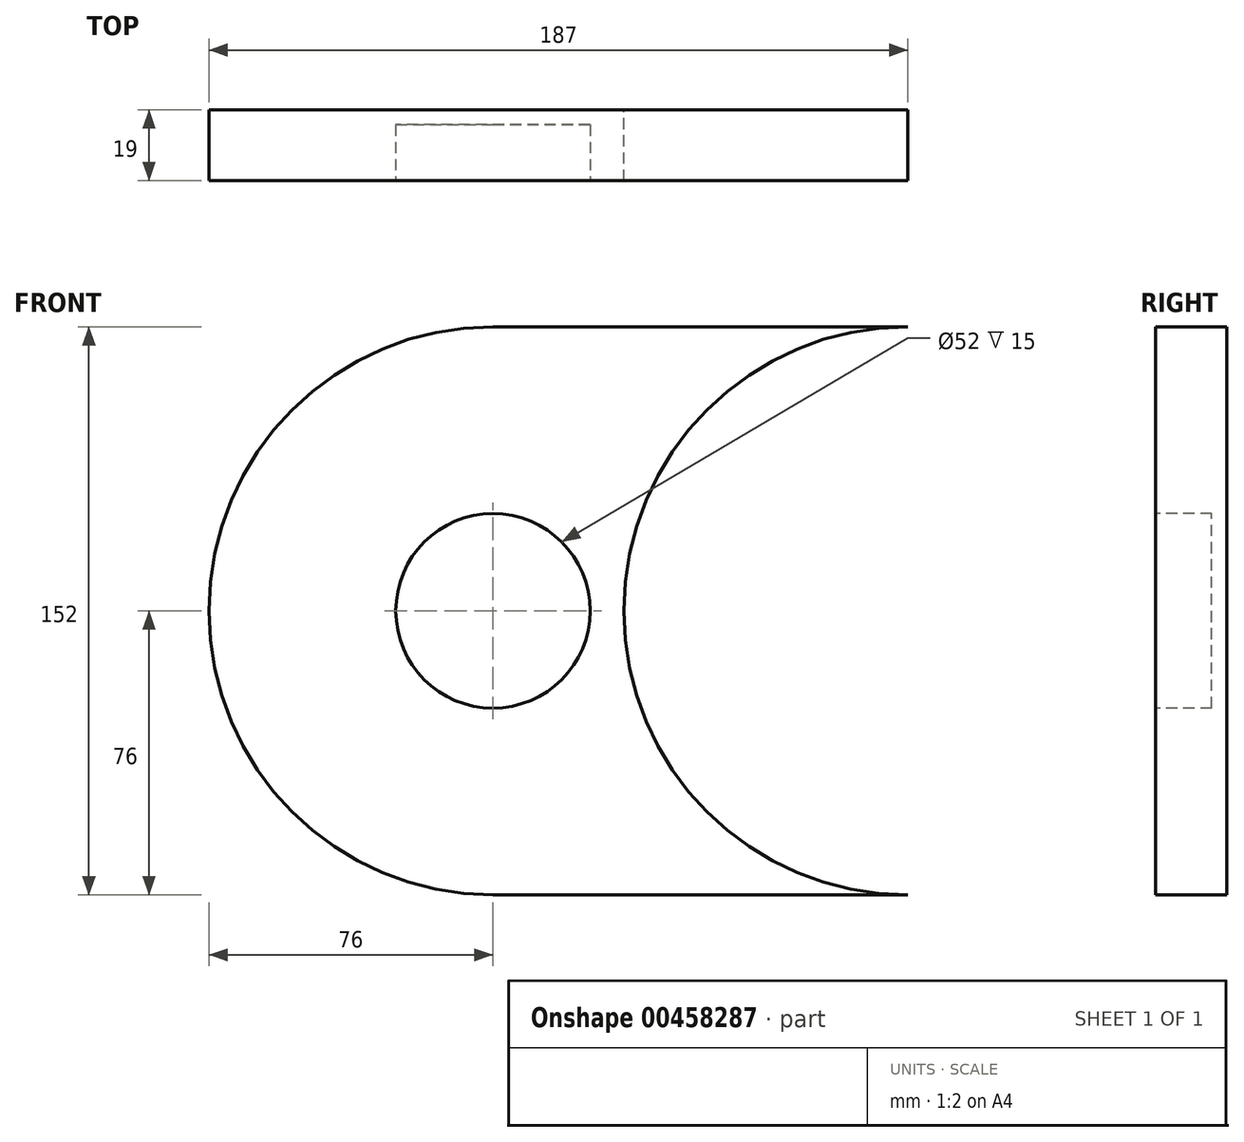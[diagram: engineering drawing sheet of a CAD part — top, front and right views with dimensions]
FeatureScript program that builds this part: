
annotation { "Feature Type Name" : "Feature", "Feature Type Description" : "" }
export const myFeature = defineFeature(function(context is Context, id is Id, definition is map)
    precondition{}
    {
        {
            var Q0;
            Q0=qCreatedBy(makeId("Front.planeOp"),FACE);
            var sketch = newSketch(context, id + "F0", { "sketchPlane" : qUnion([Q0])});
            skCircle(sketch, "E0", {"center": v(0, 0) * mm, "radius": 76 * mm});
            skCircle(sketch, "E1", {"center": v(111, 0) * mm, "radius": 76 * mm});
            skLineSegment(sketch, "E2", {"start": v(111, -76) * mm, "end": v(0, -76) * mm});
            skLineSegment(sketch, "E3", {"start": v(0, 76) * mm, "end": v(111, 76) * mm});
            skSolve(sketch);
        }
        {
            var Q0;
            {var subQ0=sQuery(id+"F0.wireOp",EDGE,"E3");Q0=makeQuery(id+"F0.imprint","IMPRINT",FACE,{"disambiguationData":[TD([[makeQuery(id+"F0.imprint","IMPRINT",EDGE,{"derivedFrom":subQ0}),-1.0]])]});}
            var Q1;
            {var subQ0=sQuery(id+"F0.wireOp",EDGE,"E2");Q1=makeQuery(id+"F0.imprint","IMPRINT",FACE,{"disambiguationData":[TD([[makeQuery(id+"F0.imprint","IMPRINT",EDGE,{"derivedFrom":subQ0}),-1.0]])]});}
            var Q2;
            {var subQ0=sQuery(id+"F0.wireOp",EDGE,"E1");var subQ1=sQuery(id+"F0.wireOp",EDGE,"E0");var subQ2=makeQuery(id+"F0.imprint","INTERSECT",VERTEX,{"disambiguationData":[OD(0.0)],"derivedFrom":[subQ1,subQ0]});Q2=makeQuery(id+"F0.imprint","IMPRINT",FACE,{"disambiguationData":[TD([[makeQuery(id+"F0.imprint","IMPRINT",EDGE,{"disambiguationData":[TD([[subQ2,1.0]])],"derivedFrom":subQ1}),1.0]])]});}
            var Q3;
            {var subQ0=sQuery(id+"F0.wireOp",EDGE,"E1");var subQ1=sQuery(id+"F0.wireOp",EDGE,"E0");var subQ2=makeQuery(id+"F0.imprint","INTERSECT",VERTEX,{"disambiguationData":[OD(0.0)],"derivedFrom":[subQ1,subQ0]});Q3=makeQuery(id+"F0.imprint","IMPRINT",FACE,{"disambiguationData":[TD([[makeQuery(id+"F0.imprint","IMPRINT",EDGE,{"disambiguationData":[TD([[subQ2,1.0]])],"derivedFrom":subQ1}),-1.0]])]});}
            var Q4;
            {var subQ0=sQuery(id+"F0.wireOp",EDGE,"E0");var subQ1=makeQuery(id+"F0.imprint","INTERSECT",VERTEX,{"derivedFrom":[subQ0,sQuery(id+"F0.wireOp",EDGE,"E3")]});Q4=makeQuery(id+"F0.imprint","IMPRINT",FACE,{"disambiguationData":[TD([[makeQuery(id+"F0.imprint","IMPRINT",EDGE,{"disambiguationData":[TD([[subQ1,1.0]])],"derivedFrom":subQ0}),1.0]])]});}
            extrude(context, id + "F1", {"entities" : qUnion([Q0, Q1, Q2, Q3, Q4]), "depth" : 50 * mm, "offsetDistance" : 25 * mm});
        }
        {
            var Q0;
            Q0=qCreatedBy(makeId("Front.planeOp"),FACE);
            cPlane(context, id + "F2", {"entities" : qUnion([Q0]), "cplaneType" : CPlaneType.OFFSET, "offset" : 19 * mm, "width" : 150 * mm, "height" : 150 * mm});
        }
        {
            var Q0;
            Q0=qCreatedBy(id+"F2.planeOp",FACE);
            var sketch = newSketch(context, id + "F3", { "sketchPlane" : qUnion([Q0])});
            skCircle(sketch, "E4", {"center": v(0, 0) * mm, "radius": 64 * mm});
            skCircle(sketch, "E5", {"center": v(111, 0) * mm, "radius": 64 * mm});
            skLineSegment(sketch, "E6", {"start": v(0, -64) * mm, "end": v(111, -64) * mm});
            skLineSegment(sketch, "E7", {"start": v(0, 64) * mm, "end": v(111, 64) * mm});
            skSolve(sketch);
        }
        {
            var Q0;
            Q0 = qSketchRegion(id + "F3", true);
            var Q1;
            Q1=makeQuery(id+"F1.opExtrude","CAP_FACE",FACE,{"disambiguationData":[OSD([sQuery(id+"F0.wireOp",EDGE,"E0"),sQuery(id+"F0.wireOp",EDGE,"E1"),sQuery(id+"F0.wireOp",EDGE,"E2"),sQuery(id+"F0.wireOp",EDGE,"E3")])],"isStart":false});
            extrude(context, id + "F4", {"entities" : qUnion([Q0, Q1]), "operationType" : NewBodyOperationType.REMOVE, "depth" : 100 * mm, "offsetDistance" : 25 * mm});
        }
        {
            var Q0;
            {var subQ0=sQuery(id+"F3.wireOp",EDGE,"E5");var subQ1=sQuery(id+"F3.wireOp",EDGE,"E4");var subQ2=makeQuery(id+"F3.imprint","INTERSECT",VERTEX,{"disambiguationData":[OD(0.0)],"derivedFrom":[subQ1,subQ0]});Q0=makeQuery(id+"F4.boolean.opBoolean","SPLIT",FACE,{"disambiguationData":[TD([makeQuery(id+"F4.opExtrude","SWEPT_FACE",FACE,{"disambiguationData":[OSD([subQ1]),TDD([makeQuery(id+"F3.imprint","IMPRINT",EDGE,{"disambiguationData":[TD([[subQ2,1.0]])],"derivedFrom":subQ1})])]})])],"derivedFrom":makeQuery(id+"F1.opExtrude","CAP_FACE",FACE,{"disambiguationData":[OSD([sQuery(id+"F0.wireOp",EDGE,"E0"),sQuery(id+"F0.wireOp",EDGE,"E1"),sQuery(id+"F0.wireOp",EDGE,"E2"),sQuery(id+"F0.wireOp",EDGE,"E3")])],"isStart":false})});}
            var Q1;
            Q1=makeQuery(id+"F4.boolean.opBoolean","COPY",FACE,{"derivedFrom":makeQuery(id+"F4.opExtrude","CAP_FACE",FACE,{"disambiguationData":[OSD([sQuery(id+"F3.wireOp",EDGE,"E4"),sQuery(id+"F3.wireOp",EDGE,"E5"),sQuery(id+"F3.wireOp",EDGE,"E6"),sQuery(id+"F3.wireOp",EDGE,"E7")])],"isStart":true})});
            extrude(context, id + "F5", {"entities" : qUnion([Q0]), "operationType" : NewBodyOperationType.REMOVE, "endBound" : BoundingType.UP_TO_SURFACE, "oppositeDirection" : true, "depth" : 25 * mm, "endBoundEntityFace" : qUnion([Q1]), "offsetDistance" : 25 * mm});
        }
        {
            var Q0;
            Q0=qCreatedBy(id+"F2.planeOp",FACE);
            var sketch = newSketch(context, id + "F6", { "sketchPlane" : qUnion([Q0])});
            skCircle(sketch, "E8", {"center": v(0, 0) * mm, "radius": 26 * mm});
            skSolve(sketch);
        }
        {
            var Q0;
            Q0 = qSketchRegion(id + "F6", true);
            extrude(context, id + "F7", {"entities" : qUnion([Q0]), "operationType" : NewBodyOperationType.REMOVE, "oppositeDirection" : true, "depth" : 15 * mm, "offsetDistance" : 25 * mm});
        }
        {
            var Q0;
            Q0=qCreatedBy(makeId("Right.planeOp"),FACE);
            cPlane(context, id + "F8", {"entities" : qUnion([Q0]), "cplaneType" : CPlaneType.OFFSET, "offset" : 111 * mm, "width" : 150 * mm, "height" : 150 * mm});
        }
        {
            var Q0;
            Q0=qCreatedBy(id+"F8.planeOp",FACE);
            var sketch = newSketch(context, id + "F9", { "sketchPlane" : qUnion([Q0])});
            skLineSegment(sketch, "E9", {"start": v(0, 0) * mm, "end": v(0, 11) * mm});
            skLineSegment(sketch, "E10", {"start": v(0, 11) * mm, "end": v(-2, 11) * mm});
            skLineSegment(sketch, "E11", {"start": v(-2, 11) * mm, "end": v(-2, 18.61) * mm});
            skLineSegment(sketch, "E12", {"start": v(-2, 18.61) * mm, "end": v(-7, 18.61) * mm});
            skLineSegment(sketch, "E13", {"start": v(-7, 18.61) * mm, "end": v(-7, 23.18) * mm});
            skLineSegment(sketch, "E14", {"start": v(-7, 23.18) * mm, "end": v(-19, 23.18) * mm});
            skLineSegment(sketch, "E15", {"start": v(-19, 23.18) * mm, "end": v(-19, 0) * mm});
            skLineSegment(sketch, "E16", {"start": v(0, 0) * mm, "end": v(-52.6, 0) * mm, "construction": true});
            skLineSegment(sketch, "E17", {"start": v(-19, 0) * mm, "end": v(0, 0) * mm});
            skSolve(sketch);
        }
        {
            var Q0;
            Q0 = qSketchRegion(id + "F9", true);
            var Q1;
            Q1=sQuery(id+"F9.wireOp",EDGE,"E16");
            revolve(context, id + "F10", {"operationType" : NewBodyOperationType.REMOVE, "entities" : qUnion([Q0]), "axis" : qUnion([Q1]), "revolveType" : RevolveType.FULL});
        }
    });
